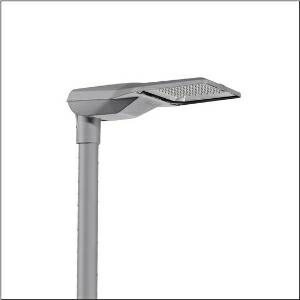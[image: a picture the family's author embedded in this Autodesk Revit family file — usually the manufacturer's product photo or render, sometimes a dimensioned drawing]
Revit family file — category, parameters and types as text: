
# Revit family: streetlight_sl_21_iq_midi___st0_8a_5xe3c61d08nb_b69d
name_source: partatom
category: Lighting Fixtures
units: mm (PartAtom-declared; Revit-internal decimal feet)

## family parameters
Cut with Voids When Loaded = No
Host = Face
Light Source = No
Part Type = Normal
Room Calculation Point = No
Round Connector Dimension = Use Diameter
Shared = No

## types (1)
- --- (1 x LED, 20820 lm, 155.5 W, 2700K)
    Apparent Load = 155 VA
    CIE Flux Codes = 41 75 97 100 100
    Color Rendering = 70
    Color Temperature = 2700K
    Default Elevation = 1800 mm
    Description = Streetlight SL 21 iQ midi, mast luminaire, primary light control with lens, of PMMA, primary optical cover: cover, of toughened safety glass, transparent, light distribution: ST0.8a, light emission: direct distribution, primary light characteristic: asymmetric, installation type: post-top, side-entry, LED, High Power LED, rated luminous flux: 20.820lm, luminous efficacy: 134lm/W, light colour: 727, colour temperature: 2700K, control gear: iQ-Comfort, control: Auto-Match, Temp-Guard, Lumen-Switch, Night-Set, Smart-Wire, Light-Fading, Desk-Remote (wireless, voltage-free reading and setting of iQ features in the workshop via application-optimized NFC function/RFID function), optimised constant luminous flux control (CLO 2.0), pre-setting: linear dimming characteristic, mains connection: 230..240V, AC, 50/60Hz, start of lifetime: 156W, end of service life: 162W, reduction: 69W, luminaire housing, of diecast aluminium, powder-coated, SITECO metallic grey (DB 702S), corrosivity category C5 high according to DIN EN ISO 12944, please order mast flange separately, inclination adjustable: 0°, 5°, 10°, 15°, sealing non-destructively replaceable, multi-level sealing system, length: 644mm, width: 335mm, height: 110mm, mast flange for spigot size: 42mm (side-entry): 5XC10008XM4, 60/48mm (side-entry/post-top): 5XC10108XM2, 76/60mm (side-entry/post-top): 5XC10108XM1, mounting height: 4..8m, protection rating (complete): IP66, insulation class (complete): insulation class II (safety insulation), certification: CE, ENEC, ENEC+, VDE, impact resistance: IK10, permissible operating ambient temperature for outdoor applications: -40..+50°C, standard-compliant lighting for roads and squares, packaging unit: 1 piece

Light Distribution: ST0.8a
    Height = 111 mm
    Lamp = 1 x LED
    Lamp Light Flux = 20820 lm
    Lamp Power = 155.5 W
    Lamp count = 1
    Length = 644 mm
    Luminous efficacy = 134 lm/W
    Manufacturer = Siteco
    ModVariant = No
    Model = 5XE3C61D08NB
    Number of Poles = 1
    OnlyDefault = Yes
    Power Factor = 1
    Product Name = Streetlight SL 21 iQ midi | ST0.8a
    Product group = mast luminaire | pylon top
    ProductGroupID = 6100
    Protection Class = Protection class II
    Protection Degree = IP 66
    RLX_Detail_Level = 1
    RLX_Emergency_Light_Flux = 0 lm
    RLX_Emergency_Type = 0
    RLX_Emergency_Type_DB = No
    RlxData = <blob elided: 27161 chars, md5=e636776d>
    Socket = socket
    Standby Power = 0 W
    System Light Flux = 20820 lm
    System Power = 155 W
    Type Comments = factory setting: luminous flux: 100 % | dim-lin: 254 | 823 mA
    Type Image = l_1004298.jpg
    URL = http://relux.com
    VarID = @adj_168313
    Voltage = 0 V
    Weight = 0.00 kg
    Width = 336 mm

## geometry (parser evidence)
native form markers: Blend x4, Sweep x11
no freeform markers — native parametric forms only
